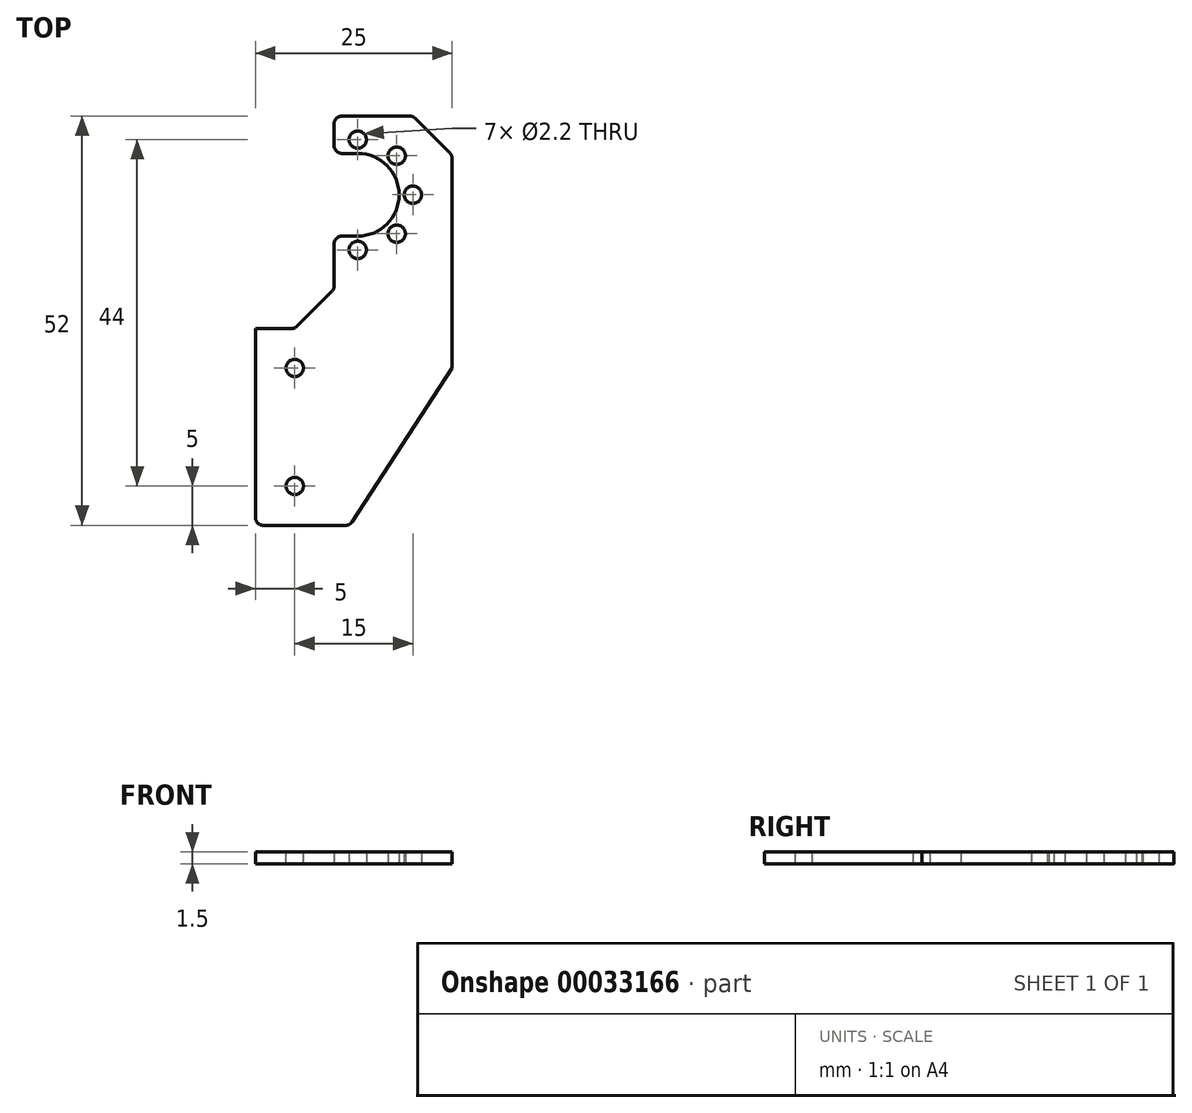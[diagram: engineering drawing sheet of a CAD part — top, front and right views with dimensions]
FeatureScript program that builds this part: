
annotation { "Feature Type Name" : "Feature", "Feature Type Description" : "" }
export const myFeature = defineFeature(function(context is Context, id is Id, definition is map)
    precondition{}
    {
        {
            var Q0;
            Q0=qCreatedBy(makeId("Top.planeOp"),FACE);
            var sketch = newSketch(context, id + "F0", { "sketchPlane" : qUnion([Q0])});
            skLineSegment(sketch, "E0.bottom", {"start": v(7.5, 55) * mm, "end": v(-7.5, 55) * mm});
            skLineSegment(sketch, "E0.top", {"start": v(7.5, -55) * mm, "end": v(-7.5, -55) * mm});
            skLineSegment(sketch, "E0.left", {"start": v(7.5, 55) * mm, "end": v(7.5, -55) * mm});
            skLineSegment(sketch, "E0.right", {"start": v(-7.5, 55) * mm, "end": v(-7.5, 50.25) * mm});
            skPoint(sketch, "E0.middle", {"position": v(0, 0) * mm});
            skArc(sketch, "E1", {"start": v(-4.5, 39.75) * mm, "mid": v(0.75, 45) * mm, "end": v(-4.5, 50.25) * mm});
            skCircle(sketch, "E2", {"center": v(-4.5, 52) * mm, "radius": 1.1 * mm});
            skCircle(sketch, "E3.4.0", {"center": v(-4.5, 38) * mm, "radius": 1.1 * mm});
            skCircle(sketch, "E3.5.0", {"center": v(0.45, 40.05) * mm, "radius": 1.1 * mm});
            skCircle(sketch, "E3.6.0", {"center": v(2.5, 45) * mm, "radius": 1.1 * mm});
            skCircle(sketch, "E3.7.0", {"center": v(0.45, 49.95) * mm, "radius": 1.1 * mm});
            skLineSegment(sketch, "E4", {"start": v(-4.5, 50.25) * mm, "end": v(-7.5, 50.25) * mm});
            skLineSegment(sketch, "E5", {"start": v(-4.5, 39.75) * mm, "end": v(-7.5, 39.75) * mm});
            skLineSegment(sketch, "E6.trimOffspring", {"start": v(-7.5, 39.75) * mm, "end": v(-7.5, 28) * mm});
            skLineSegment(sketch, "E7.bottom", {"start": v(-7.5, -55) * mm, "end": v(-42.5, -55) * mm});
            skLineSegment(sketch, "E7.top", {"start": v(-7.5, 28) * mm, "end": v(-42.5, 28) * mm});
            skLineSegment(sketch, "E7.left", {"start": v(-7.5, -55) * mm, "end": v(-7.5, 28) * mm, "construction": true});
            skLineSegment(sketch, "E7.right", {"start": v(-42.5, -55) * mm, "end": v(-42.5, 28) * mm});
            skSolve(sketch);
        }
        {
            var Q0;
            Q0 = qSketchRegion(id + "F0", true);
            extrude(context, id + "F1", {"entities" : qUnion([Q0]), "depth" : 1.5 * mm});
        }
        {
            var Q0;
            Q0=makeQuery(id+"F1.opExtrude","CAP_FACE",FACE,{"disambiguationData":[OSD([sQuery(id+"F0.wireOp",EDGE,"E0.bottom"),sQuery(id+"F0.wireOp",EDGE,"E0.top"),sQuery(id+"F0.wireOp",EDGE,"E0.left"),sQuery(id+"F0.wireOp",EDGE,"E0.right"),sQuery(id+"F0.wireOp",EDGE,"E1"),sQuery(id+"F0.wireOp",EDGE,"E2"),sQuery(id+"F0.wireOp",EDGE,"E3.4.0"),sQuery(id+"F0.wireOp",EDGE,"E3.5.0"),sQuery(id+"F0.wireOp",EDGE,"E3.6.0"),sQuery(id+"F0.wireOp",EDGE,"E3.7.0"),sQuery(id+"F0.wireOp",EDGE,"E4"),sQuery(id+"F0.wireOp",EDGE,"E5"),sQuery(id+"F0.wireOp",EDGE,"E6.trimOffspring"),sQuery(id+"F0.wireOp",EDGE,"E7.bottom"),sQuery(id+"F0.wireOp",EDGE,"E7.top"),sQuery(id+"F0.wireOp",EDGE,"E7.right")])],"isStart":false});
            var sketch = newSketch(context, id + "F2", { "sketchPlane" : qUnion([Q0])});
            skLineSegment(sketch, "E8", {"start": v(7.5, 23) * mm, "end": v(-5.5, 3) * mm});
            skLineSegment(sketch, "E9", {"start": v(-5.5, 3) * mm, "end": v(-17.5, 3) * mm});
            skLineSegment(sketch, "E10", {"start": v(-17.5, 3) * mm, "end": v(-17.5, 28) * mm});
            skLineSegment(sketch, "E11", {"start": v(-12.5, 28) * mm, "end": v(-12.5, 3) * mm, "construction": true});
            skCircle(sketch, "E12", {"center": v(-12.5, 23) * mm, "radius": 1.1 * mm});
            skCircle(sketch, "E13", {"center": v(-12.5, 8) * mm, "radius": 1.1 * mm});
            skSolve(sketch);
        }
        {
            var Q0;
            {var subQ2=sQuery(id+"F2.wireOp",EDGE,"E8");Q0=makeQuery(id+"F2.imprint","IMPRINT",FACE,{"disambiguationData":[TD([[makeQuery(id+"F2.imprint","IMPRINT",EDGE,{"derivedFrom":subQ2}),1.0]])]});}
            var Q1;
            Q1=makeQuery(id+"F2.imprint","IMPRINT",FACE,{"disambiguationData":[TD([[makeQuery(id+"F2.imprint","IMPRINT",EDGE,{"derivedFrom":sQuery(id+"F2.wireOp",EDGE,"E12")}),1.0]])]});
            var Q2;
            Q2=makeQuery(id+"F2.imprint","IMPRINT",FACE,{"disambiguationData":[TD([[makeQuery(id+"F2.imprint","IMPRINT",EDGE,{"derivedFrom":sQuery(id+"F2.wireOp",EDGE,"E13")}),1.0]])]});
            extrude(context, id + "F3", {"entities" : qUnion([Q0, Q1, Q2]), "operationType" : NewBodyOperationType.REMOVE, "endBound" : BoundingType.UP_TO_NEXT, "oppositeDirection" : true, "depth" : 25 * mm});
        }
        {
            var Q0;
            Q0=makeQuery(id+"F3.boolean.opBoolean","COPY",EDGE,{"derivedFrom":makeQuery(id+"F3.opExtrude","SWEPT_EDGE",EDGE,{"disambiguationData":[OSD([sQuery(id+"F2.wireOp",EDGE,"E9"),sQuery(id+"F2.wireOp",EDGE,"E10")])]})});
            var Q1;
            Q1=makeQuery(id+"F3.boolean.opBoolean","COPY",EDGE,{"derivedFrom":makeQuery(id+"F3.opExtrude","SWEPT_EDGE",EDGE,{"disambiguationData":[OSD([sQuery(id+"F2.wireOp",EDGE,"E8"),sQuery(id+"F2.wireOp",EDGE,"E9")])]})});
            var Q2;
            Q2=makeQuery(id+"F3.boolean.opBoolean","COPY",EDGE,{"derivedFrom":makeQuery(id+"F3.opExtrude","SWEPT_EDGE",EDGE,{"disambiguationData":[OSD([sQuery(id+"F0.wireOp",EDGE,"E0.left"),sQuery(id+"F2.wireOp",EDGE,"E8")])]})});
            var Q3;
            Q3=makeQuery(id+"F1.opExtrude","SWEPT_EDGE",EDGE,{"disambiguationData":[OSD([sQuery(id+"F0.wireOp",EDGE,"E0.right"),sQuery(id+"F0.wireOp",EDGE,"E4")])]});
            var Q4;
            Q4=makeQuery(id+"F1.opExtrude","SWEPT_EDGE",EDGE,{"disambiguationData":[OSD([sQuery(id+"F0.wireOp",EDGE,"E0.bottom"),sQuery(id+"F0.wireOp",EDGE,"E0.right")])]});
            var Q5;
            Q5=makeQuery(id+"F1.opExtrude","SWEPT_EDGE",EDGE,{"disambiguationData":[OSD([sQuery(id+"F0.wireOp",EDGE,"E5"),sQuery(id+"F0.wireOp",EDGE,"E6.trimOffspring")])]});
            var Q6;
            Q6=makeQuery(id+"F3.boolean.opBoolean","COPY",EDGE,{"derivedFrom":makeQuery(id+"F3.opExtrude","SWEPT_EDGE",EDGE,{"disambiguationData":[OSD([sQuery(id+"F0.wireOp",EDGE,"E7.top"),sQuery(id+"F2.wireOp",EDGE,"E10")])]})});
            fillet(context, id + "F4", {"entities" : qUnion([Q0, Q1, Q2, Q3, Q4, Q5, Q6]), "radius" : 1 * mm, "tangentPropagation" : true, "allowEdgeOverflow" : false});
        }
        {
            var Q0;
            Q0=makeQuery(id+"F1.opExtrude","SWEPT_EDGE",EDGE,{"disambiguationData":[OSD([sQuery(id+"F0.wireOp",EDGE,"E0.bottom"),sQuery(id+"F0.wireOp",EDGE,"E0.left")])]});
            var Q1;
            Q1=makeQuery(id+"F1.opExtrude","SWEPT_EDGE",EDGE,{"disambiguationData":[OSD([sQuery(id+"F0.wireOp",EDGE,"E6.trimOffspring"),sQuery(id+"F0.wireOp",EDGE,"E7.top")])]});
            chamfer(context, id + "F5", {"entities" : qUnion([Q0, Q1]), "width" : 5 * mm, "tangentPropagation" : true});
        }
        {
            var Q0;
            {var subQ0=sQuery(id+"F0.wireOp",EDGE,"E6.trimOffspring");Q0=makeQuery(id+"F5.opChamfer","BLEND_EDGE",EDGE,{"blendedFrom":[makeQuery(id+"F1.opExtrude","SWEPT_EDGE",EDGE,{"disambiguationData":[OSD([subQ0,sQuery(id+"F0.wireOp",EDGE,"E7.top")])]}),makeQuery(id+"F1.opExtrude","SWEPT_FACE",FACE,{"disambiguationData":[OSD([subQ0])]})],"blendedInto":[makeQuery(id+"F1.opExtrude","SWEPT_FACE",FACE,{"disambiguationData":[OSD([subQ0])]})]});}
            var Q1;
            {var subQ0=sQuery(id+"F0.wireOp",EDGE,"E7.top");Q1=makeQuery(id+"F5.opChamfer","BLEND_EDGE",EDGE,{"blendedFrom":[makeQuery(id+"F1.opExtrude","SWEPT_EDGE",EDGE,{"disambiguationData":[OSD([sQuery(id+"F0.wireOp",EDGE,"E6.trimOffspring"),subQ0])]}),makeQuery(id+"F1.opExtrude","SWEPT_FACE",FACE,{"disambiguationData":[OSD([subQ0])]})],"blendedInto":[makeQuery(id+"F1.opExtrude","SWEPT_FACE",FACE,{"disambiguationData":[OSD([subQ0])]})]});}
            var Q2;
            {var subQ0=sQuery(id+"F0.wireOp",EDGE,"E0.bottom");Q2=makeQuery(id+"F5.opChamfer","BLEND_EDGE",EDGE,{"blendedFrom":[makeQuery(id+"F1.opExtrude","SWEPT_EDGE",EDGE,{"disambiguationData":[OSD([subQ0,sQuery(id+"F0.wireOp",EDGE,"E0.left")])]}),makeQuery(id+"F1.opExtrude","SWEPT_FACE",FACE,{"disambiguationData":[OSD([subQ0])]})],"blendedInto":[makeQuery(id+"F1.opExtrude","SWEPT_FACE",FACE,{"disambiguationData":[OSD([subQ0])]})]});}
            var Q3;
            {var subQ0=sQuery(id+"F0.wireOp",EDGE,"E0.left");Q3=makeQuery(id+"F5.opChamfer","BLEND_EDGE",EDGE,{"blendedFrom":[makeQuery(id+"F1.opExtrude","SWEPT_EDGE",EDGE,{"disambiguationData":[OSD([sQuery(id+"F0.wireOp",EDGE,"E0.bottom"),subQ0])]}),makeQuery(id+"F1.opExtrude","SWEPT_FACE",FACE,{"disambiguationData":[OSD([subQ0])]})],"blendedInto":[makeQuery(id+"F1.opExtrude","SWEPT_FACE",FACE,{"disambiguationData":[OSD([subQ0])]})]});}
            fillet(context, id + "F6", {"entities" : qUnion([Q0, Q1, Q2, Q3]), "radius" : 1 * mm, "tangentPropagation" : true, "allowEdgeOverflow" : false});
        }
    });
